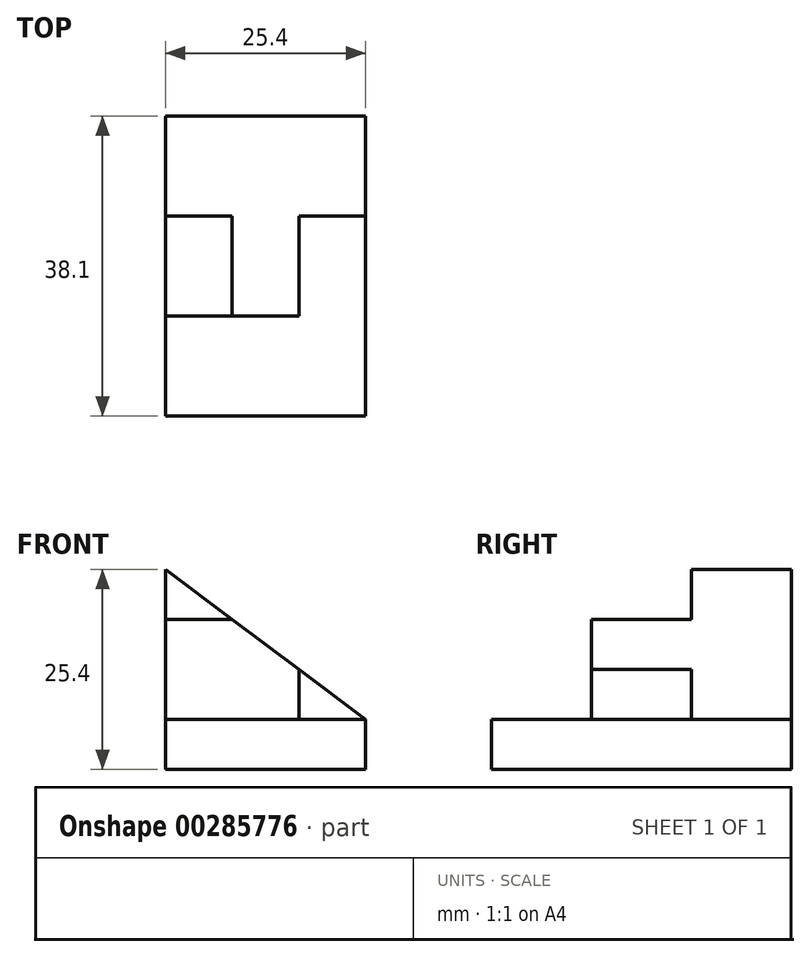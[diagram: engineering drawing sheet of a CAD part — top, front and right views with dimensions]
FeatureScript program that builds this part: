
annotation { "Feature Type Name" : "Feature", "Feature Type Description" : "" }
export const myFeature = defineFeature(function(context is Context, id is Id, definition is map)
    precondition{}
    {
        {
            var Q0;
            Q0=qCreatedBy(makeId("Front.planeOp"),FACE);
            var sketch = newSketch(context, id + "F0", { "sketchPlane" : qUnion([Q0])});
            skLineSegment(sketch, "E0", {"start": v(0, 0) * mm, "end": v(25.4, 0) * mm});
            skLineSegment(sketch, "E1", {"start": v(25.4, 0) * mm, "end": v(25.4, 6.35) * mm});
            skLineSegment(sketch, "E2", {"start": v(25.4, 6.35) * mm, "end": v(0, 25.4) * mm});
            skLineSegment(sketch, "E3", {"start": v(0, 25.4) * mm, "end": v(0, 0) * mm});
            skLineSegment(sketch, "E4", {"start": v(0, 0) * mm, "end": v(0, 6.35) * mm});
            skLineSegment(sketch, "E5", {"start": v(0, 6.35) * mm, "end": v(25.4, 6.35) * mm});
            skLineSegment(sketch, "E6", {"start": v(16.93, 12.7) * mm, "end": v(16.93, 6.35) * mm});
            skLineSegment(sketch, "E7", {"start": v(0, 19.05) * mm, "end": v(8.47, 19.05) * mm});
            skSolve(sketch);
        }
        {
            var Q0;
            {var subQ0=sQuery(id+"F0.wireOp",EDGE,"E6");Q0=makeQuery(id+"F0.imprint","IMPRINT",FACE,{"disambiguationData":[TD([[makeQuery(id+"F0.imprint","IMPRINT",EDGE,{"derivedFrom":subQ0}),-1.0]])]});}
            var Q1;
            {var subQ3=sQuery(id+"F0.wireOp",EDGE,"E7");Q1=makeQuery(id+"F0.imprint","IMPRINT",FACE,{"disambiguationData":[TD([[makeQuery(id+"F0.imprint","IMPRINT",EDGE,{"derivedFrom":subQ3}),1.0]])]});}
            var Q2;
            Q2=makeQuery(id+"F0.imprint","IMPRINT",FACE,{"disambiguationData":[TD([[makeQuery(id+"F0.imprint","IMPRINT",EDGE,{"derivedFrom":sQuery(id+"F0.wireOp",EDGE,"E0")}),1.0]])]});
            var Q3;
            {var subQ3=sQuery(id+"F0.wireOp",EDGE,"E6");Q3=makeQuery(id+"F0.imprint","IMPRINT",FACE,{"disambiguationData":[TD([[makeQuery(id+"F0.imprint","IMPRINT",EDGE,{"derivedFrom":subQ3}),1.0]])]});}
            extrude(context, id + "F1", {"entities" : qUnion([Q0, Q1, Q2, Q3]), "oppositeDirection" : true, "depth" : 38.1 * mm});
        }
        {
            var Q0;
            {var subQ3=sQuery(id+"F0.wireOp",EDGE,"E7");Q0=makeQuery(id+"F0.imprint","IMPRINT",FACE,{"disambiguationData":[TD([[makeQuery(id+"F0.imprint","IMPRINT",EDGE,{"derivedFrom":subQ3}),1.0]])]});}
            extrude(context, id + "F2", {"entities" : qUnion([Q0]), "operationType" : NewBodyOperationType.REMOVE, "oppositeDirection" : true, "depth" : 25.4 * mm});
        }
        {
            var Q0;
            {var subQ0=sQuery(id+"F0.wireOp",EDGE,"E6");Q0=makeQuery(id+"F0.imprint","IMPRINT",FACE,{"disambiguationData":[TD([[makeQuery(id+"F0.imprint","IMPRINT",EDGE,{"derivedFrom":subQ0}),-1.0]])]});}
            extrude(context, id + "F3", {"entities" : qUnion([Q0]), "operationType" : NewBodyOperationType.REMOVE, "oppositeDirection" : true, "depth" : 12.7 * mm});
        }
        {
            var Q0;
            {var subQ3=sQuery(id+"F0.wireOp",EDGE,"E6");Q0=makeQuery(id+"F0.imprint","IMPRINT",FACE,{"disambiguationData":[TD([[makeQuery(id+"F0.imprint","IMPRINT",EDGE,{"derivedFrom":subQ3}),1.0]])]});}
            extrude(context, id + "F4", {"entities" : qUnion([Q0]), "operationType" : NewBodyOperationType.REMOVE, "oppositeDirection" : true, "depth" : 25.4 * mm});
        }
    });
